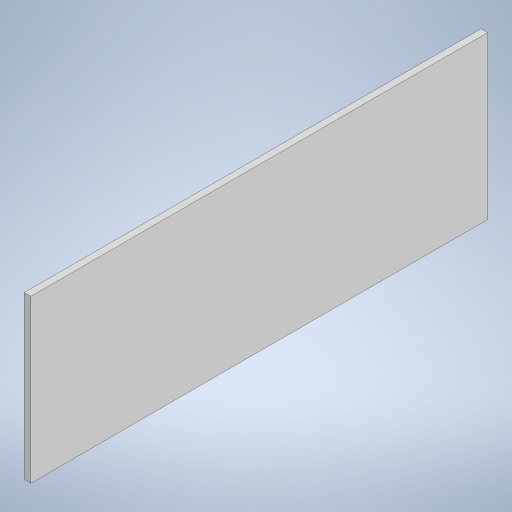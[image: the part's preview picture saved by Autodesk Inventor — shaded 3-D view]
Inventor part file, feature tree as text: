
AUTODESK INVENTOR PART (.ipt)
format: ipt  version: 2024.3 (Build 283343000, 343)  size: 190,464 bytes
history: native  units: mm
features: extrude x1, sketch x1
ambient origin geometry x8: Origin, YZ Plane, XZ Plane, XY Plane, X Axis, Y Axis, Z Axis, Center Point
bodies: Solid1 (feature_tree)
feature tree (2):
  extrude  "Extrusion1"  Depth=206.0mm
  sketch  "Sketch1"  dims[d0=73.0mm d1=206.0mm d2=3.0mm d3=0.0mm]
